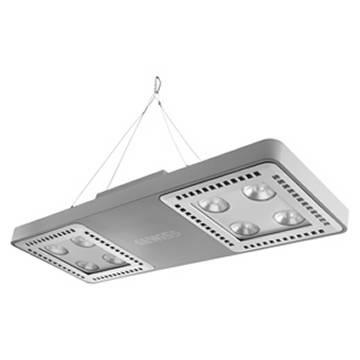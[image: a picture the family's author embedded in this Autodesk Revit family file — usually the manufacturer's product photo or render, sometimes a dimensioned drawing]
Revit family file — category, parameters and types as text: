
# Revit family: LigULing-Industrial-GEWISS-SMART[4]UL_HIGHBAYS-LED_2M
name_source: partatom
category: Apparecchi per illuminazione
units: mm (PartAtom-declared; Revit-internal decimal feet)

## family parameters
Basato su piano di lavoro = Sì
Condiviso = No
Numero OmniClass = 23.80.70.00
Punto di calcolo locali = No
Quota connettore circolare = Usa diametro
Sempre verticale = No
Sorgente d'illuminazione = No
Taglio con vuoti quando caricato = No
Tipo di parte = Normale
Titolo OmniClass = Lighting

## types (6) — shared parameters
Application = Internal
Body = PA6 "Halogen Free" loaded fibreglass
Carico apparente = 97 VA
Catalogue = LIGHTING
Classification: = -
Classificazione = Lighting
Color Rendering Index = CRI-80
Colour = Grey RAL 7035
Colour : = Grey RAL 7035
Commenti sul wattaggio = 97W
Context = Logistics and industrial manufacturing lighting
Control System = ON / OFF
Control System : = ON / OFF
DIN 18032-3 certification = -
Device with reduced surface temperature = Yes
Dist_sorg_lum = 10 mm  [stored 0.0328084 ft]
Driver = Included
Driver Box = Built-in
Electrocod = 2444
Eletrical and lighting features = -
External screw = Stainless steel
Fixing = -
Gasket = anti-aging silicone
General information = -
Glow Wire Test : = 850 °C
IDF = efad7fad-bc59-42f2-b2a0-928aa5b78dfc
IDT = 05376d21caf540b985b33c65cc7972c3
IP degree = IP66
IPEA = -
Immagine tipo = GWL1311.jpg
Installationa and maintenance = -
Insulation class = I
LED Maintenance = Non-replaceable
Lampada = LED
Larghezza = 254 mm
Lifetime = L90B10 (Tq+25°C) = 100.000 h - L90B10 (Tq+40°C) = 50.000 h
Locking Hook = -
Luminaire = LED Industrial ReflectorÂ
Lunghezza = 699 mm  [stored 2.29331 ft]
Mascherina = <Per categoria>
Materials = -
Maximum surface exposed to the wind : = 0,184 m²
Motore = <Per categoria>
Mouting and installation = Ceiling - Wallmounting - Suspension
Operating temperature : = -25°C / +40 °C
Optic Maintenance = Non-replaceable
Optic and illuminating features = -
Overvoltage protection = DM 6 kV / CM 10 kV
Photobiological Risk Class = RG0
Produttore = GEWISS S.p.A.
Prospetto di default = 1219 mm
Rated frequency (Hz) = 50/60 Hz
Shield type = Tempered glass Thickness 4mm
Shock resistance = IK08
Spessore plafoniera = 40 mm
Standard Deviation Colour Matching = SDCM = 3
Standard- = UL 1598 - CSA C22.2 No. 250.0-18
Standards and approvals = -
Stocking temperature = -
Struttura plafoniera = <Per categoria>
Supply voltage = 120-277 V
System power = 129W
Technical sheet = https://www.gewiss.com
Tilt- = With bracket accessory
Trasformatore = <Per categoria>
Type of light source = LED - Not replaceable
URL = https://www.gewiss.com
Unique digital code (Datamatrix) = Datamatrix
Version file RFA = 20.11
Voltaggio = 230 V
Warranty = 5 years
Weight (kg): = 6,5
Wiring = Single wiring with anti-breathing cable exiting metallic PG (NO Connector)

## per-type parameters (varying)
| type | Colour temperature | Descrizione | Efficiency (lm/W) | Lumen output (lm) | Modello | Optic | Optic : | SEO | Unified Glare Rating |
| GWS4220GP857 - SMART4HB 2M ST.AL.ON/OFF UL 90° 57K | 5700K | SMART[4]HB 2M ST.AL.ON/OFF UL 90° 57K | 138 | 17800 | GWS4220GP857 | 90° | Metallic PC reflector and PMMA lenses |  | UGR - 25 |
| GWS4220GA857 - SMART4HB 2M ST.AL.ON/OFF UL ARR.57K | 5700K | SMART[4]HB 2M ST.AL.ON/OFF UL ARR.57K | 136 | 17500 | GWS4220GA857 | Array | Metallized polycarbonate reflector | High bay | UGR - 25 |
| GWS4220GH857 - SMART4HB 2M ST.AL.ON/OFF UL 60° 57K | 5700K | SMART[4]HB 2M ST.AL.ON/OFF UL 60° 57K | 136 | 17500 | GWS4220GH857 | 60° | Metallic PC reflector and PMMA lenses |  | UGR - 22 |
| GWS4220GA840 - SMART4HB 2M ST.AL.ON/OFF UL ARR.40K | 4000K | SMART[4]HB 2M ST.AL.ON/OFF UL ARR.40K | 136 | 17500 | GWS4220GA840 | Array | Metallized polycarbonate reflector | High bay | UGR - 25 |
| GWS4220GP840 - SMART4HB 2M ST.AL.ON/OFF UL 90° 40K | 4000K | SMART[4]HB 2M ST.AL.ON/OFF UL 90° 40K | 138 | 17800 | GWS4220GP840 | 90° | Metallic PC reflector and PMMA lenses |  | UGR - 25 |
| GWS4220GH840 - SMART4HB 2M ST.AL.ON/OFF UL 60° 40K | 4000K | SMART[4]HB 2M ST.AL.ON/OFF UL 60° 40K | 136 | 17500 | GWS4220GH840 | 60° | Metallic PC reflector and PMMA lenses |  | UGR - 22 |

note: [stored X ft] marks values corroborated as IEEE doubles in the binary element streams (Revit-internal decimal feet)

## geometry (parser evidence)
native form markers: Blend x4, Sweep x3
no freeform markers — native parametric forms only
